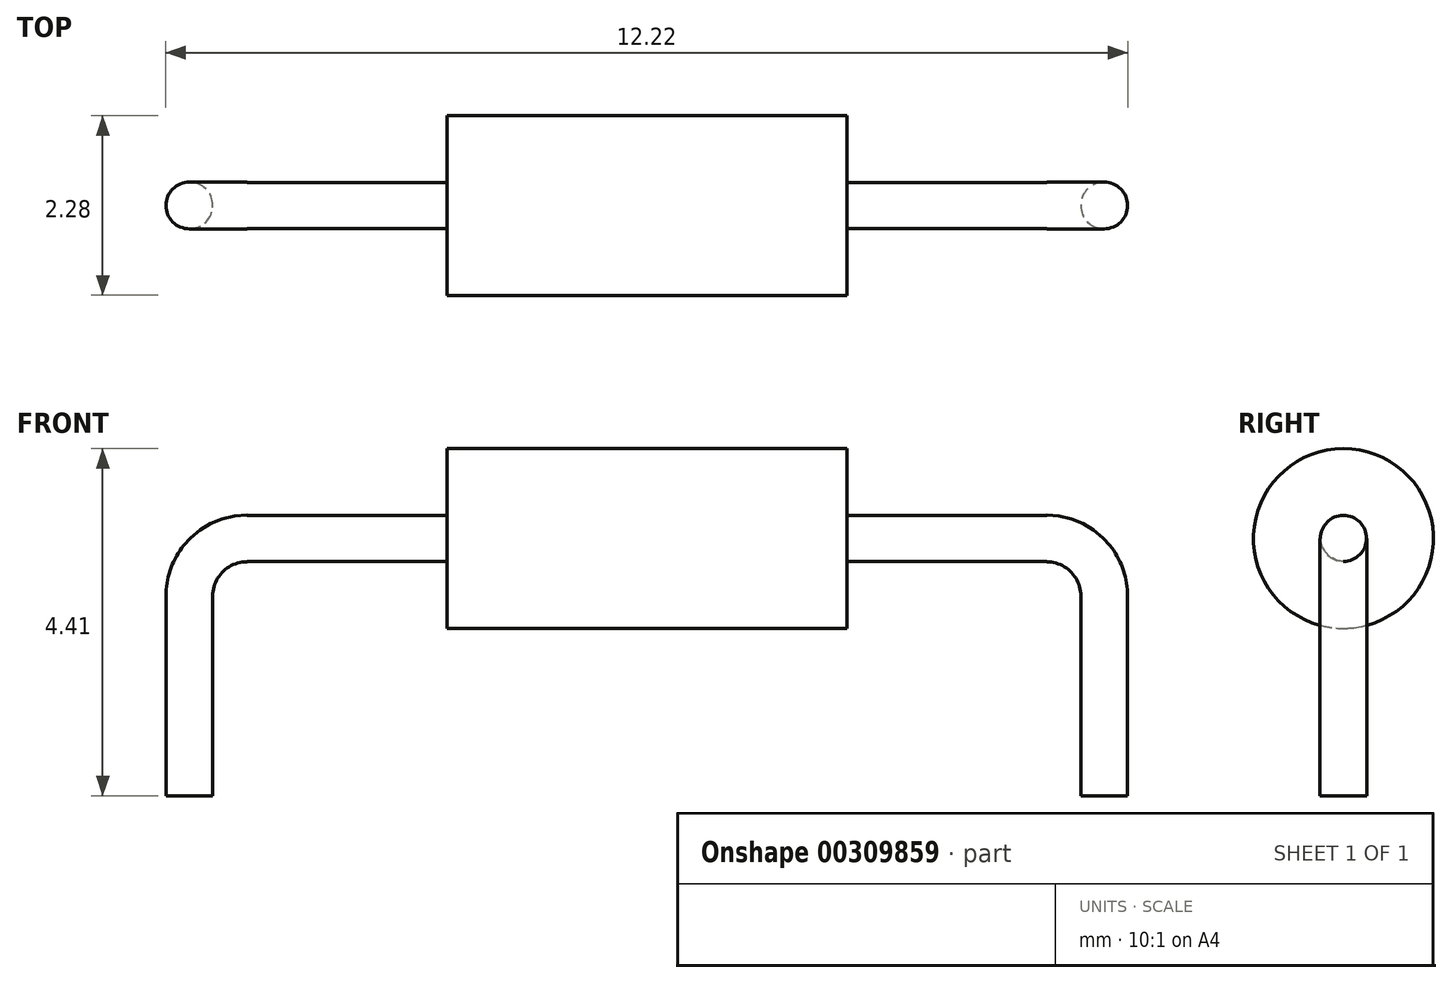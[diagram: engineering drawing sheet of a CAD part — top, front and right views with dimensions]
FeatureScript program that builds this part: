
annotation { "Feature Type Name" : "Feature", "Feature Type Description" : "" }
export const myFeature = defineFeature(function(context is Context, id is Id, definition is map)
    precondition{}
    {
        {
            var Q0;
            Q0=qCreatedBy(makeId("Right.planeOp"),FACE);
            var sketch = newSketch(context, id + "F0", { "sketchPlane" : qUnion([Q0])});
            skCircle(sketch, "E0", {"center": v(0, 0) * mm, "radius": 1.14 * mm});
            skSolve(sketch);
        }
        {
            var Q0;
            Q0 = qSketchRegion(id + "F0", true);
            extrude(context, id + "F1", {"entities" : qUnion([Q0]), "endBound" : BoundingType.SYMMETRIC, "depth" : 5.08 * mm});
        }
        {
            var Q0;
            Q0=makeQuery(id+"F1.opExtrude","CAP_FACE",FACE,{"disambiguationData":[OSD([sQuery(id+"F0.wireOp",EDGE,"E0")])],"isStart":false});
            var sketch = newSketch(context, id + "F2", { "sketchPlane" : qUnion([Q0])});
            skCircle(sketch, "E1", {"center": v(0, 0) * mm, "radius": 0.3 * mm});
            skSolve(sketch);
        }
        {
            var Q0;
            Q0=qCreatedBy(makeId("Right.planeOp"),FACE);
            cPlane(context, id + "F3", {"entities" : qUnion([Q0]), "cplaneType" : CPlaneType.OFFSET, "offset" : 5.08 * mm, "width" : 152.4 * mm, "height" : 152.4 * mm});
        }
        {
            var Q0;
            Q0 = qSketchRegion(id + "F2", true);
            var Q1;
            Q1=qCreatedBy(id+"F3.planeOp",FACE);
            extrude(context, id + "F4", {"entities" : qUnion([Q0]), "endBound" : BoundingType.UP_TO_SURFACE, "endBoundEntityFace" : qUnion([Q1]), "depth" : 25.4 * mm});
        }
        {
            var Q0;
            Q0=makeQuery(id+"F4.opExtrude","CAP_FACE",FACE,{"disambiguationData":[OSD([sQuery(id+"F2.wireOp",EDGE,"E1")])],"isStart":false});
            var sketch = newSketch(context, id + "F5", { "sketchPlane" : qUnion([Q0])});
            skCircle(sketch, "E2", {"center": v(0, 0) * mm, "radius": 0.3 * mm});
            skSolve(sketch);
        }
        {
            var Q0;
            Q0=qCreatedBy(id+"F3.planeOp",FACE);
            var sketch = newSketch(context, id + "F6", { "sketchPlane" : qUnion([Q0])});
            skLineSegment(sketch, "E3", {"start": v(-2.19, -0.73) * mm, "end": v(2.93, -0.73) * mm, "construction": true});
            skSolve(sketch);
        }
        {
            var Q0;
            Q0=makeQuery(id+"F5.imprint","IMPRINT",FACE,{"disambiguationData":[TD([[makeQuery(id+"F5.imprint","IMPRINT",EDGE,{"derivedFrom":makeQuery(id+"F4.opExtrude","CAP_EDGE",EDGE,{"disambiguationData":[OSD([sQuery(id+"F2.wireOp",EDGE,"E1")])],"isStart":false})}),1.0]])]});
            var sketch = newSketch(context, id + "F7", { "sketchPlane" : qUnion([Q0])});
            skCircle(sketch, "E4", {"center": v(0, 0) * mm, "radius": 0.3 * mm});
            skSolve(sketch);
        }
        {
            var Q0;
            Q0 = qSketchRegion(id + "F7", true);
            var Q1;
            Q1=sQuery(id+"F6.wireOp",EDGE,"E3");
            revolve(context, id + "F8", {"operationType" : NewBodyOperationType.ADD, "entities" : qUnion([Q0]), "axis" : qUnion([Q1]), "revolveType" : RevolveType.ONE_DIRECTION, "angle" : 90 * degree});
        }
        {
            var Q0;
            Q0=makeQuery(id+"F8.opRevolve","CAP_FACE",FACE,{"disambiguationData":[OSD([sQuery(id+"F7.wireOp",EDGE,"E4")])],"isStart":false});
            var sketch = newSketch(context, id + "F9", { "sketchPlane" : qUnion([Q0])});
            skCircle(sketch, "E5", {"center": v(5.8, 0) * mm, "radius": 0.3 * mm});
            skSolve(sketch);
        }
        {
            var Q0;
            Q0 = qSketchRegion(id + "F9", true);
            extrude(context, id + "F10", {"entities" : qUnion([Q0]), "operationType" : NewBodyOperationType.ADD, "depth" : 2.54 * mm});
        }
        {
            var Q0;
            Q0=makeQuery(id+"F4.opExtrude","SWEPT_BODY",BODY,{"disambiguationData":[OSD([sQuery(id+"F2.wireOp",EDGE,"E1")])]});
            var Q1;
            Q1=qCreatedBy(makeId("Right.planeOp"),FACE);
            mirror(context, id + "F11", {"operationType" : NewBodyOperationType.ADD, "entities" : qUnion([Q0]), "mirrorPlane" : qUnion([Q1])});
        }
    });
